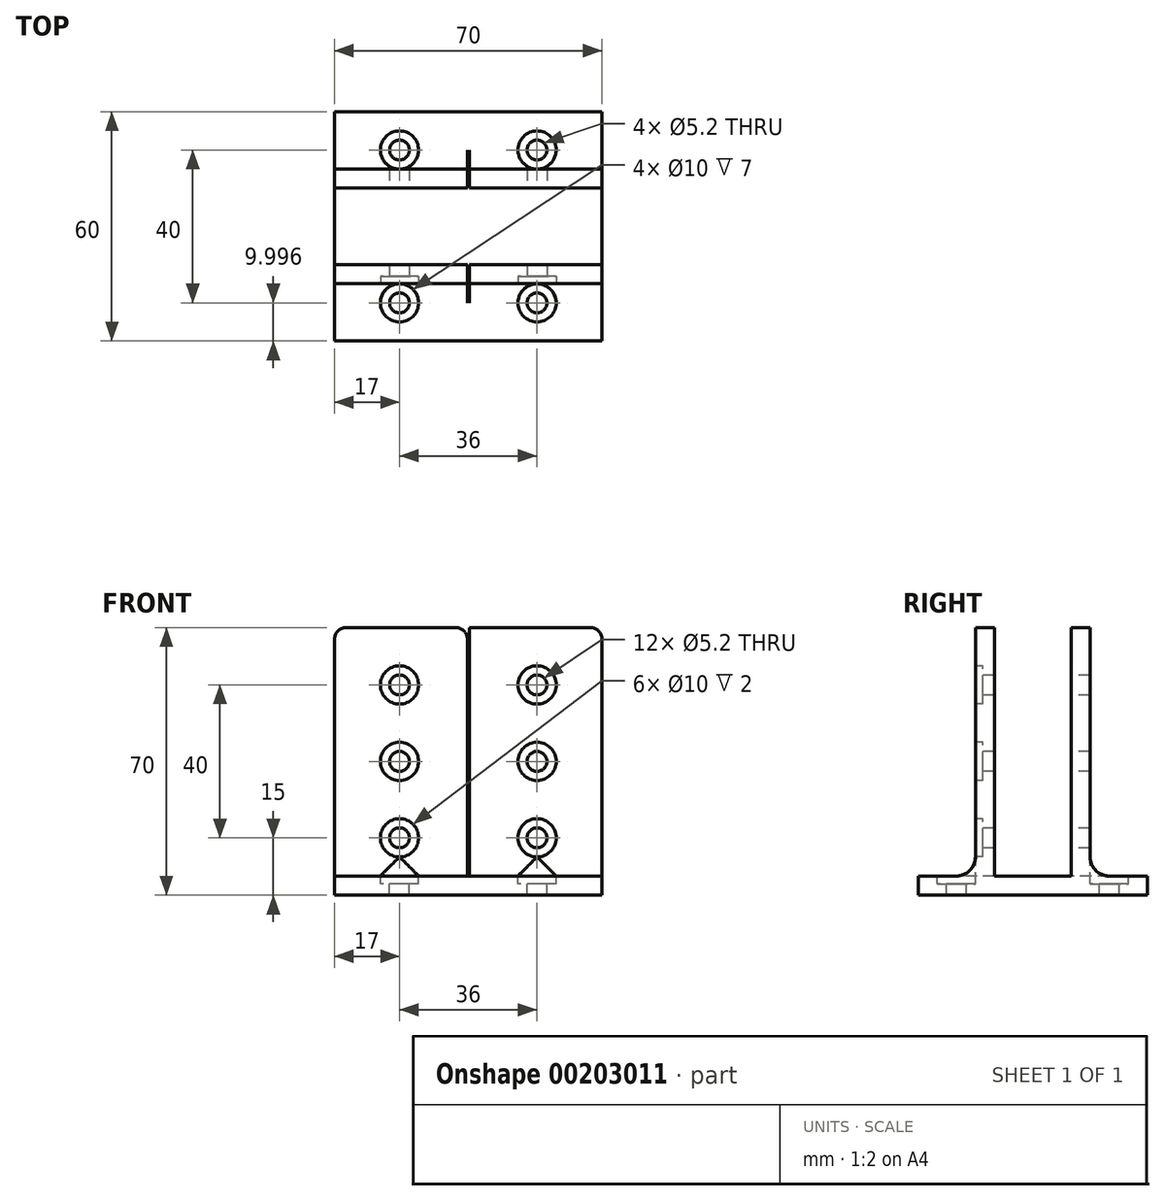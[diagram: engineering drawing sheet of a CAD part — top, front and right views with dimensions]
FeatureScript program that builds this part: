
annotation { "Feature Type Name" : "Feature", "Feature Type Description" : "" }
export const myFeature = defineFeature(function(context is Context, id is Id, definition is map)
    precondition{}
    {
        {
            var Q0;
            Q0=qCreatedBy(makeId("Right.planeOp"),FACE);
            var sketch = newSketch(context, id + "F0", { "sketchPlane" : qUnion([Q0])});
            skLineSegment(sketch, "E0.bottom", {"start": v(-10.96, 0) * mm, "end": v(4.04, 0) * mm});
            skLineSegment(sketch, "E0.left", {"start": v(-10.96, 0) * mm, "end": v(-10.96, -5) * mm});
            skLineSegment(sketch, "E1.top", {"start": v(34.04, 65) * mm, "end": v(29.04, 65) * mm});
            skLineSegment(sketch, "E1.left", {"start": v(34.04, 0) * mm, "end": v(34.04, 65) * mm});
            skLineSegment(sketch, "E1.right", {"start": v(29.04, 0) * mm, "end": v(29.04, 65) * mm});
            skLineSegment(sketch, "E2.top", {"start": v(9.04, 65) * mm, "end": v(4.04, 65) * mm});
            skLineSegment(sketch, "E2.left", {"start": v(9.04, 0) * mm, "end": v(9.04, 65) * mm});
            skLineSegment(sketch, "E2.right", {"start": v(4.04, 0) * mm, "end": v(4.04, 65) * mm});
            skLineSegment(sketch, "E3.trimOffspring", {"start": v(9.04, 0) * mm, "end": v(29.04, 0) * mm});
            skLineSegment(sketch, "E4.bottom", {"start": v(34.04, 0) * mm, "end": v(49.04, 0) * mm});
            skLineSegment(sketch, "E4.right", {"start": v(49.04, 0) * mm, "end": v(49.04, -5) * mm});
            skLineSegment(sketch, "E5", {"start": v(-10.96, -5) * mm, "end": v(49.04, -5) * mm});
            skSolve(sketch);
        }
        {
            var Q0;
            Q0 = qSketchRegion(id + "F0", true);
            extrude(context, id + "F1", {"entities" : qUnion([Q0]), "depth" : 70 * mm});
        }
        {
            var Q0;
            Q0=makeQuery(id+"F1.opExtrude","SWEPT_FACE",FACE,{"disambiguationData":[OSD([sQuery(id+"F0.wireOp",EDGE,"E2.right")])]});
            var sketch = newSketch(context, id + "F2", { "sketchPlane" : qUnion([Q0])});
            skLineSegment(sketch, "E6.0", {"start": v(70, 65) * mm, "end": v(0, 65) * mm, "construction": true});
            skPoint(sketch, "E7", {"position": v(35, 65) * mm});
            skLineSegment(sketch, "E8.bottom", {"start": v(34.75, 0) * mm, "end": v(35.25, 0) * mm});
            skLineSegment(sketch, "E8.top", {"start": v(34.75, 65) * mm, "end": v(35.25, 65) * mm});
            skLineSegment(sketch, "E8.left", {"start": v(34.75, 0) * mm, "end": v(34.75, 65) * mm});
            skLineSegment(sketch, "E8.right", {"start": v(35.25, 0) * mm, "end": v(35.25, 65) * mm});
            skLineSegment(sketch, "E9", {"start": v(0, 50) * mm, "end": v(70, 50) * mm, "construction": true});
            skLineSegment(sketch, "E10", {"start": v(0, 10) * mm, "end": v(70, 10) * mm, "construction": true});
            skLineSegment(sketch, "E11", {"start": v(0, 30) * mm, "end": v(70, 30) * mm, "construction": true});
            skPoint(sketch, "E12", {"position": v(17, 50) * mm});
            skPoint(sketch, "E13", {"position": v(17, 30) * mm});
            skPoint(sketch, "E14", {"position": v(17, 10) * mm});
            skPoint(sketch, "E15", {"position": v(53, 50) * mm});
            skPoint(sketch, "E16", {"position": v(53, 30) * mm});
            skPoint(sketch, "E17", {"position": v(53, 10) * mm});
            skSolve(sketch);
        }
        {
            var Q0;
            Q0=makeQuery(id+"F2.imprint","IMPRINT",FACE,{"disambiguationData":[TD([[makeQuery(id+"F2.imprint","IMPRINT",EDGE,{"derivedFrom":sQuery(id+"F2.wireOp",EDGE,"E8.bottom")}),-1.0]])]});
            extrude(context, id + "F3", {"entities" : qUnion([Q0]), "operationType" : NewBodyOperationType.REMOVE, "endBound" : BoundingType.THROUGH_ALL, "oppositeDirection" : true, "depth" : 25 * mm});
        }
        {
            var Q0;
            Q0=makeQuery(id+"F3.boolean.opBoolean","MERGE",FACE,{"derivedFrom":[makeQuery(id+"F1.opExtrude","SWEPT_FACE",FACE,{"disambiguationData":[OSD([sQuery(id+"F0.wireOp",EDGE,"E0.bottom")])]}),makeQuery(id+"F1.opExtrude","SWEPT_FACE",FACE,{"disambiguationData":[OSD([sQuery(id+"F0.wireOp",EDGE,"E3.trimOffspring")])]}),makeQuery(id+"F1.opExtrude","SWEPT_FACE",FACE,{"disambiguationData":[OSD([sQuery(id+"F0.wireOp",EDGE,"E4.bottom")])]}),makeQuery(id+"F3.opExtrude","SWEPT_FACE",FACE,{"disambiguationData":[OSD([sQuery(id+"F2.wireOp",EDGE,"E8.bottom")])]})]});
            var sketch = newSketch(context, id + "F4", { "sketchPlane" : qUnion([Q0])});
            skLineSegment(sketch, "E18", {"start": v(53, 49.04) * mm, "end": v(53, -10.96) * mm, "construction": true});
            skLineSegment(sketch, "E19", {"start": v(17, 49.04) * mm, "end": v(17, -10.96) * mm, "construction": true});
            skPoint(sketch, "E20", {"position": v(53, 39.04) * mm});
            skPoint(sketch, "E21", {"position": v(17, 39.04) * mm});
            skPoint(sketch, "E22", {"position": v(17, 29.04) * mm});
            skPoint(sketch, "E23", {"position": v(53, -0.96) * mm});
            skPoint(sketch, "E23.positionSnap0", {"position": v(34.75, 6.54) * mm});
            skPoint(sketch, "E24", {"position": v(17, -0.96) * mm});
            skSolve(sketch);
        }
        {
            var Q0;
            Q0=sQuery(id+"F4.wireOp",VERTEX,"E24");
            var Q1;
            Q1=sQuery(id+"F4.wireOp",VERTEX,"E23");
            var Q2;
            Q2=sQuery(id+"F4.wireOp",VERTEX,"E20");
            var Q3;
            Q3=sQuery(id+"F4.wireOp",VERTEX,"E21");
            var Q4;
            Q4=makeQuery(id+"F1.opExtrude","SWEPT_BODY",BODY,{"disambiguationData":[OSD([sQuery(id+"F0.wireOp",EDGE,"E0.bottom"),sQuery(id+"F0.wireOp",EDGE,"E0.left"),sQuery(id+"F0.wireOp",EDGE,"E1.top"),sQuery(id+"F0.wireOp",EDGE,"E1.left"),sQuery(id+"F0.wireOp",EDGE,"E1.right"),sQuery(id+"F0.wireOp",EDGE,"E2.top"),sQuery(id+"F0.wireOp",EDGE,"E2.left"),sQuery(id+"F0.wireOp",EDGE,"E2.right"),sQuery(id+"F0.wireOp",EDGE,"E3.trimOffspring"),sQuery(id+"F0.wireOp",EDGE,"E4.bottom"),sQuery(id+"F0.wireOp",EDGE,"E4.right"),sQuery(id+"F0.wireOp",EDGE,"E5")])]});
            hole(context, id + "F5", {"style" : HoleStyle.C_BORE, "endStyle" : HoleEndStyle.THROUGH, "holeDiameter" : 5.2 * mm, "cBoreDiameter" : 10 * mm, "cBoreDepth" : 2 * mm, "startFromSketch" : true, "locations" : qUnion([Q0, Q1, Q2, Q3]), "scope" : qUnion([Q4]), "isTappedThrough" : true});
        }
        {
            var Q0;
            {var subQ0=sQuery(id+"F0.wireOp",EDGE,"E2.top");var subQ1=sQuery(id+"F0.wireOp",EDGE,"E2.right");var subQ2=sQuery(id+"F2.wireOp",EDGE,"E8.left");Q0=makeQuery(id+"F3.boolean.opBoolean","COPY",EDGE,{"disambiguationData":[TD([makeQuery(id+"F1.opExtrude","SWEPT_FACE",FACE,{"disambiguationData":[OSD([subQ0])]})])],"derivedFrom":makeQuery(id+"F3.opExtrude","SWEPT_EDGE",EDGE,{"disambiguationData":[OSD([subQ0,subQ1,sQuery(id+"F2.wireOp",EDGE,"E8.top"),subQ2])]})});}
            var Q1;
            {var subQ0=sQuery(id+"F0.wireOp",EDGE,"E2.top");var subQ1=sQuery(id+"F0.wireOp",EDGE,"E2.right");var subQ2=sQuery(id+"F2.wireOp",EDGE,"E8.right");Q1=makeQuery(id+"F3.boolean.opBoolean","COPY",EDGE,{"disambiguationData":[TD([makeQuery(id+"F1.opExtrude","SWEPT_FACE",FACE,{"disambiguationData":[OSD([subQ0])]})])],"derivedFrom":makeQuery(id+"F3.opExtrude","SWEPT_EDGE",EDGE,{"disambiguationData":[OSD([subQ0,subQ1,sQuery(id+"F2.wireOp",EDGE,"E8.top"),subQ2])]})});}
            var Q2;
            {var subQ0=sQuery(id+"F2.wireOp",EDGE,"E8.right");Q2=makeQuery(id+"F3.boolean.opBoolean","COPY",EDGE,{"disambiguationData":[TD([makeQuery(id+"F1.opExtrude","SWEPT_FACE",FACE,{"disambiguationData":[OSD([sQuery(id+"F0.wireOp",EDGE,"E1.top")])]})])],"derivedFrom":makeQuery(id+"F3.opExtrude","SWEPT_EDGE",EDGE,{"disambiguationData":[OSD([sQuery(id+"F0.wireOp",EDGE,"E2.top"),sQuery(id+"F0.wireOp",EDGE,"E2.right"),sQuery(id+"F2.wireOp",EDGE,"E8.top"),subQ0])]})});}
            var Q3;
            {var subQ0=sQuery(id+"F2.wireOp",EDGE,"E8.left");Q3=makeQuery(id+"F3.boolean.opBoolean","COPY",EDGE,{"disambiguationData":[TD([makeQuery(id+"F1.opExtrude","SWEPT_FACE",FACE,{"disambiguationData":[OSD([sQuery(id+"F0.wireOp",EDGE,"E1.top")])]})])],"derivedFrom":makeQuery(id+"F3.opExtrude","SWEPT_EDGE",EDGE,{"disambiguationData":[OSD([sQuery(id+"F0.wireOp",EDGE,"E2.top"),sQuery(id+"F0.wireOp",EDGE,"E2.right"),sQuery(id+"F2.wireOp",EDGE,"E8.top"),subQ0])]})});}
            var Q4;
            Q4=makeQuery(id+"F1.opExtrude","CAP_EDGE",EDGE,{"disambiguationData":[OSD([sQuery(id+"F0.wireOp",EDGE,"E2.top")])],"isStart":false});
            var Q5;
            Q5=makeQuery(id+"F1.opExtrude","CAP_EDGE",EDGE,{"disambiguationData":[OSD([sQuery(id+"F0.wireOp",EDGE,"E1.top")])],"isStart":false});
            var Q6;
            Q6=makeQuery(id+"F1.opExtrude","CAP_EDGE",EDGE,{"disambiguationData":[OSD([sQuery(id+"F0.wireOp",EDGE,"E2.top")])],"isStart":true});
            var Q7;
            Q7=makeQuery(id+"F1.opExtrude","CAP_EDGE",EDGE,{"disambiguationData":[OSD([sQuery(id+"F0.wireOp",EDGE,"E1.top")])],"isStart":true});
            fillet(context, id + "F6", {"entities" : qUnion([Q0, Q1, Q2, Q3, Q4, Q5, Q6, Q7]), "radius" : 3 * mm, "tangentPropagation" : true, "allowEdgeOverflow" : false});
        }
        {
            var Q0;
            {var subQ1=sQuery(id+"F0.wireOp",EDGE,"E2.right");var subQ3=sQuery(id+"F0.wireOp",EDGE,"E0.bottom");Q0=makeQuery(id+"F3.boolean.opBoolean","SPLIT",EDGE,{"disambiguationData":[TD([makeQuery(id+"F3.opExtrude","SWEPT_FACE",FACE,{"disambiguationData":[OSD([sQuery(id+"F2.wireOp",EDGE,"E8.left")])]})])],"derivedFrom":makeQuery(id+"F1.opExtrude","SWEPT_EDGE",EDGE,{"disambiguationData":[OSD([subQ3,subQ1])]})});}
            var Q1;
            {var subQ1=sQuery(id+"F0.wireOp",EDGE,"E2.right");var subQ3=sQuery(id+"F0.wireOp",EDGE,"E0.bottom");Q1=makeQuery(id+"F3.boolean.opBoolean","SPLIT",EDGE,{"disambiguationData":[TD([makeQuery(id+"F3.opExtrude","SWEPT_FACE",FACE,{"disambiguationData":[OSD([sQuery(id+"F2.wireOp",EDGE,"E8.right")])]})])],"derivedFrom":makeQuery(id+"F1.opExtrude","SWEPT_EDGE",EDGE,{"disambiguationData":[OSD([subQ3,subQ1])]})});}
            var Q2;
            {var subQ1=sQuery(id+"F0.wireOp",EDGE,"E1.left");var subQ2=sQuery(id+"F0.wireOp",EDGE,"E4.bottom");Q2=makeQuery(id+"F3.boolean.opBoolean","SPLIT",EDGE,{"disambiguationData":[TD([makeQuery(id+"F3.opExtrude","SWEPT_FACE",FACE,{"disambiguationData":[OSD([sQuery(id+"F2.wireOp",EDGE,"E8.right")])]})])],"derivedFrom":makeQuery(id+"F1.opExtrude","SWEPT_EDGE",EDGE,{"disambiguationData":[OSD([subQ1,subQ2])]})});}
            var Q3;
            {var subQ1=sQuery(id+"F0.wireOp",EDGE,"E1.left");var subQ2=sQuery(id+"F0.wireOp",EDGE,"E4.bottom");Q3=makeQuery(id+"F3.boolean.opBoolean","SPLIT",EDGE,{"disambiguationData":[TD([makeQuery(id+"F3.opExtrude","SWEPT_FACE",FACE,{"disambiguationData":[OSD([sQuery(id+"F2.wireOp",EDGE,"E8.left")])]})])],"derivedFrom":makeQuery(id+"F1.opExtrude","SWEPT_EDGE",EDGE,{"disambiguationData":[OSD([subQ1,subQ2])]})});}
            fillet(context, id + "F7", {"entities" : qUnion([Q0, Q1, Q2, Q3]), "radius" : 5 * mm, "tangentPropagation" : true, "allowEdgeOverflow" : false});
        }
        {
            var Q0;
            Q0=sQuery(id+"F2.wireOp",VERTEX,"E12");
            var Q1;
            Q1=sQuery(id+"F2.wireOp",VERTEX,"E13");
            var Q2;
            Q2=sQuery(id+"F2.wireOp",VERTEX,"E14");
            var Q3;
            Q3=sQuery(id+"F2.wireOp",VERTEX,"E15");
            var Q4;
            Q4=sQuery(id+"F2.wireOp",VERTEX,"E16");
            var Q5;
            Q5=sQuery(id+"F2.wireOp",VERTEX,"E17");
            var Q6;
            Q6=makeQuery(id+"F1.opExtrude","SWEPT_BODY",BODY,{"disambiguationData":[OSD([sQuery(id+"F0.wireOp",EDGE,"E0.bottom"),sQuery(id+"F0.wireOp",EDGE,"E0.left"),sQuery(id+"F0.wireOp",EDGE,"E1.top"),sQuery(id+"F0.wireOp",EDGE,"E1.left"),sQuery(id+"F0.wireOp",EDGE,"E1.right"),sQuery(id+"F0.wireOp",EDGE,"E2.top"),sQuery(id+"F0.wireOp",EDGE,"E2.left"),sQuery(id+"F0.wireOp",EDGE,"E2.right"),sQuery(id+"F0.wireOp",EDGE,"E3.trimOffspring"),sQuery(id+"F0.wireOp",EDGE,"E4.bottom"),sQuery(id+"F0.wireOp",EDGE,"E4.right"),sQuery(id+"F0.wireOp",EDGE,"E5")])]});
            hole(context, id + "F8", {"style" : HoleStyle.C_BORE, "endStyle" : HoleEndStyle.THROUGH, "holeDiameter" : 5.2 * mm, "cBoreDiameter" : 10 * mm, "cBoreDepth" : 2 * mm, "startFromSketch" : true, "locations" : qUnion([Q0, Q1, Q2, Q3, Q4, Q5]), "scope" : qUnion([Q6]), "isTappedThrough" : true});
        }
    });
